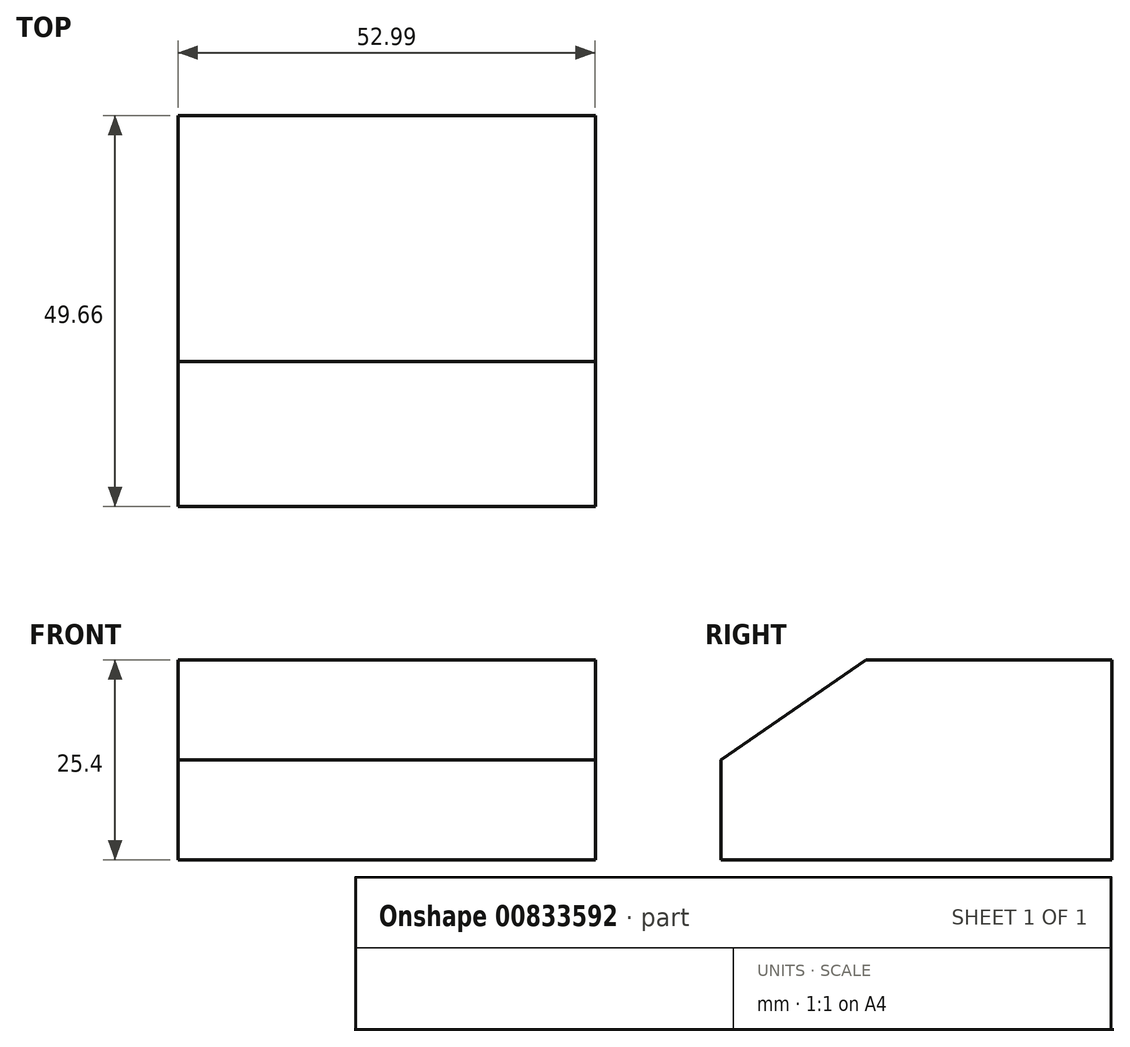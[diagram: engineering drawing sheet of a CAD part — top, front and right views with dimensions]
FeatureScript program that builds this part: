
annotation { "Feature Type Name" : "Feature", "Feature Type Description" : "" }
export const myFeature = defineFeature(function(context is Context, id is Id, definition is map)
    precondition{}
    {
        {
            var Q0;
            Q0=qCreatedBy(makeId("Top.planeOp"),FACE);
            var sketch = newSketch(context, id + "F0", { "sketchPlane" : qUnion([Q0])});
            skLineSegment(sketch, "E0.bottom", {"start": v(0, 0) * mm, "end": v(53, 0) * mm});
            skLineSegment(sketch, "E0.top", {"start": v(0, -49.66) * mm, "end": v(53, -49.66) * mm});
            skLineSegment(sketch, "E0.left", {"start": v(0, 0) * mm, "end": v(0, -49.66) * mm});
            skLineSegment(sketch, "E0.right", {"start": v(53, 0) * mm, "end": v(53, -49.66) * mm});
            skSolve(sketch);
        }
        {
            var Q0;
            Q0 = qSketchRegion(id + "F0", true);
            extrude(context, id + "F1", {"entities" : qUnion([Q0]), "depth" : 25.4 * mm, "offsetDistance" : 25.4 * mm});
        }
        {
            var Q0;
            Q0=makeQuery(id+"F1.opExtrude","SWEPT_FACE",FACE,{"disambiguationData":[OSD([sQuery(id+"F0.wireOp",EDGE,"E0.right")])]});
            var sketch = newSketch(context, id + "F2", { "sketchPlane" : qUnion([Q0])});
            skLineSegment(sketch, "E1.0", {"start": v(-49.66, 25.4) * mm, "end": v(-49.66, 12.7) * mm});
            skLineSegment(sketch, "E2.0", {"start": v(-31.26, 25.4) * mm, "end": v(-49.66, 25.4) * mm});
            skLineSegment(sketch, "E3", {"start": v(-49.66, 12.7) * mm, "end": v(-31.26, 25.4) * mm});
            skPoint(sketch, "E4.orphan", {"position": v(0, 25.4) * mm});
            skPoint(sketch, "E5.orphan", {"position": v(-49.66, 0) * mm});
            skSolve(sketch);
        }
        {
            var Q0;
            Q0=makeQuery(id+"F2.imprint","IMPRINT",FACE,{"disambiguationData":[TD([[makeQuery(id+"F2.imprint","IMPRINT",EDGE,{"derivedFrom":sQuery(id+"F2.wireOp",EDGE,"E1.0")}),1.0]])]});
            extrude(context, id + "F3", {"entities" : qUnion([Q0]), "operationType" : NewBodyOperationType.REMOVE, "oppositeDirection" : true, "depth" : 104.4 * mm, "offsetDistance" : 25.4 * mm});
        }
    });
